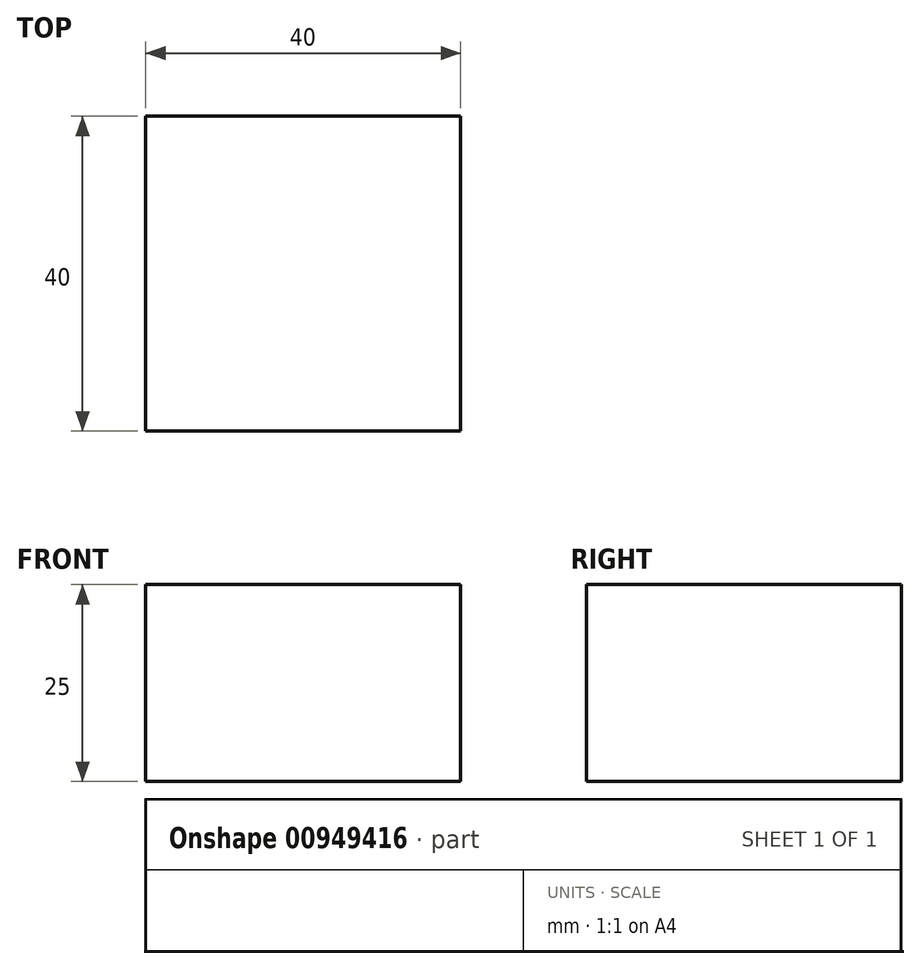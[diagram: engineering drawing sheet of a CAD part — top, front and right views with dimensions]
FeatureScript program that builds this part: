
annotation { "Feature Type Name" : "Feature", "Feature Type Description" : "" }
export const myFeature = defineFeature(function(context is Context, id is Id, definition is map)
    precondition{}
    {
        {
            var Q0;
            Q0=qCreatedBy(makeId("Top.planeOp"),FACE);
            var sketch = newSketch(context, id + "F0", { "sketchPlane" : qUnion([Q0])});
            skLineSegment(sketch, "E0.bottom", {"start": v(-20, -20) * mm, "end": v(20, -20) * mm});
            skLineSegment(sketch, "E0.top", {"start": v(-20, 20) * mm, "end": v(20, 20) * mm});
            skLineSegment(sketch, "E0.left", {"start": v(-20, -20) * mm, "end": v(-20, 20) * mm});
            skLineSegment(sketch, "E0.right", {"start": v(20, -20) * mm, "end": v(20, 20) * mm});
            skPoint(sketch, "E0.middle", {"position": v(0, 0) * mm});
            skSolve(sketch);
        }
        {
            var Q0;
            Q0=makeQuery(id+"F0.imprint","IMPRINT",FACE,{"disambiguationData":[TD([[makeQuery(id+"F0.imprint","IMPRINT",EDGE,{"derivedFrom":sQuery(id+"F0.wireOp",EDGE,"E0.bottom")}),1.0]])]});
            extrude(context, id + "F1", {"entities" : qUnion([Q0]), "depth" : 25 * mm, "offsetDistance" : 25 * mm});
        }
    });
